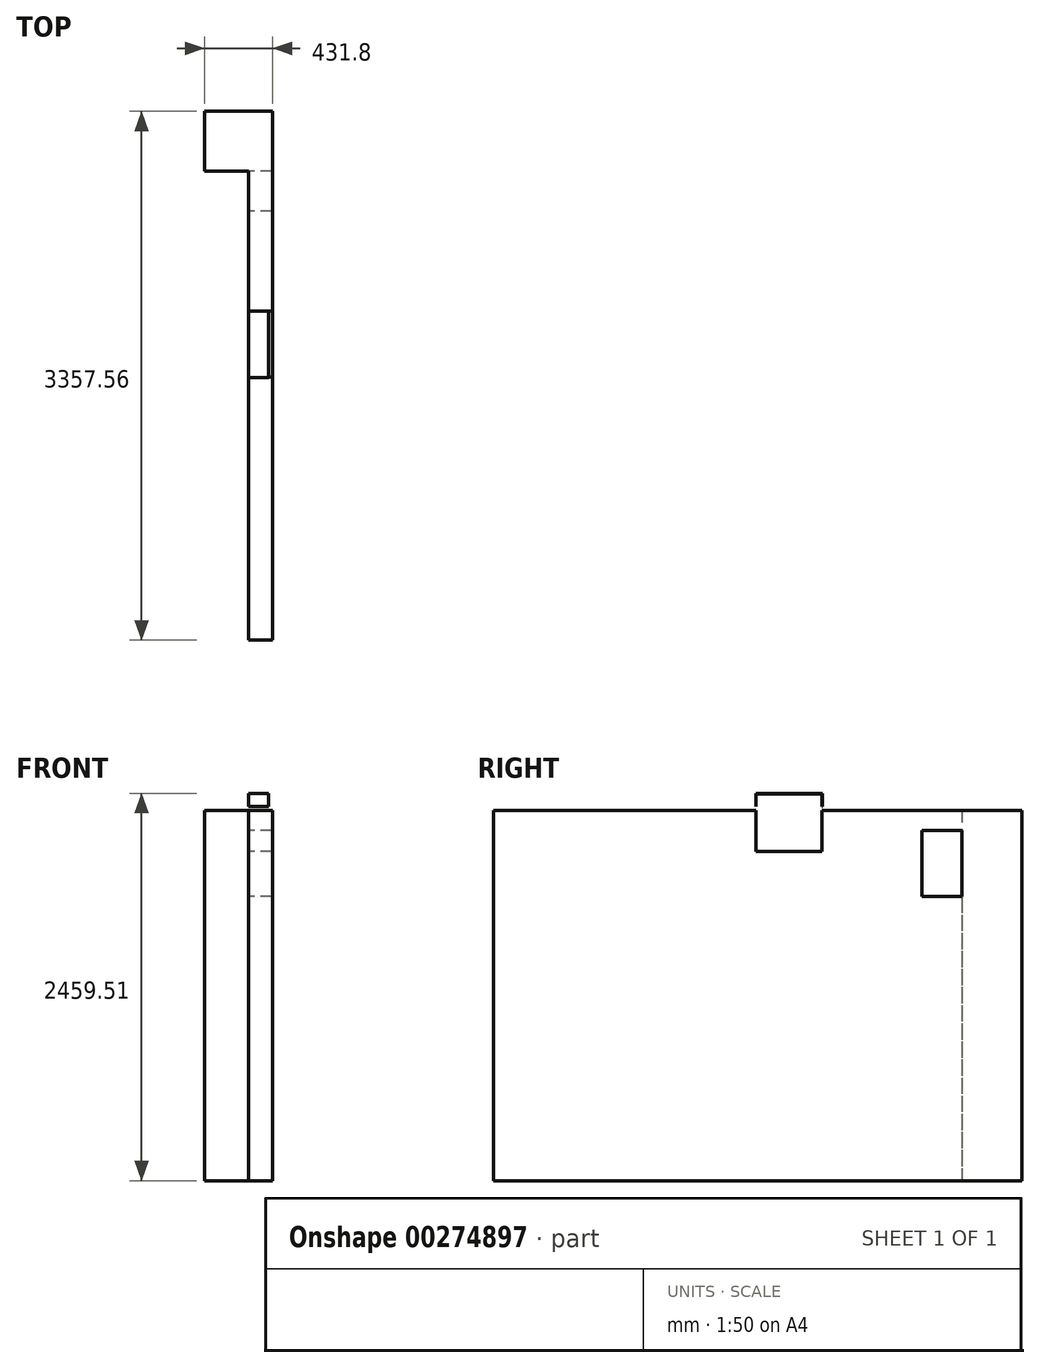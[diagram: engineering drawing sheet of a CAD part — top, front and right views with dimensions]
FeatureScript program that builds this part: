
annotation { "Feature Type Name" : "Feature", "Feature Type Description" : "" }
export const myFeature = defineFeature(function(context is Context, id is Id, definition is map)
    precondition{}
    {
        {
            var Q0;
            Q0=qCreatedBy(makeId("Top.planeOp"),FACE);
            var sketch = newSketch(context, id + "F0", { "sketchPlane" : qUnion([Q0])});
            skLineSegment(sketch, "E0.bottom", {"start": v(0, 0) * mm, "end": v(18288, 0) * mm});
            skLineSegment(sketch, "E0.top", {"start": v(0, 5486.4) * mm, "end": v(18288, 5486.4) * mm});
            skLineSegment(sketch, "E0.left", {"start": v(0, 0) * mm, "end": v(0, 5486.4) * mm});
            skLineSegment(sketch, "E0.right", {"start": v(18288, 0) * mm, "end": v(18288, 5486.4) * mm});
            skSolve(sketch);
        }
        {
            var Q0;
            Q0=makeQuery(id+"F0.imprint","IMPRINT",FACE,{"disambiguationData":[TD([[makeQuery(id+"F0.imprint","IMPRINT",EDGE,{"derivedFrom":sQuery(id+"F0.wireOp",EDGE,"E0.bottom")}),1.0]])]});
            extrude(context, id + "F1", {"entities" : qUnion([Q0]), "depth" : 101.6 * mm});
        }
        {
            var Q0;
            Q0=makeQuery(id+"F1.opExtrude","CAP_FACE",FACE,{"disambiguationData":[OSD([sQuery(id+"F0.wireOp",EDGE,"E0.bottom"),sQuery(id+"F0.wireOp",EDGE,"E0.top"),sQuery(id+"F0.wireOp",EDGE,"E0.left"),sQuery(id+"F0.wireOp",EDGE,"E0.right")])],"isStart":false});
            var sketch = newSketch(context, id + "F2", { "sketchPlane" : qUnion([Q0])});
            skLineSegment(sketch, "E1.bottom", {"start": v(18288, 5486.4) * mm, "end": v(13335, 5486.4) * mm, "construction": true});
            skLineSegment(sketch, "E1.top", {"start": v(18288, 2128.84) * mm, "end": v(13335, 2128.84) * mm, "construction": true});
            skLineSegment(sketch, "E1.left", {"start": v(18288, 5486.4) * mm, "end": v(18288, 2128.84) * mm, "construction": true});
            skLineSegment(sketch, "E1.right", {"start": v(13335, 5486.4) * mm, "end": v(13335, 2128.84) * mm, "construction": true});
            skLineSegment(sketch, "E2.bottom", {"start": v(18288, 2128.84) * mm, "end": v(13335, 2128.84) * mm});
            skLineSegment(sketch, "E2.top", {"start": v(18288, 1976.44) * mm, "end": v(13335, 1976.44) * mm});
            skLineSegment(sketch, "E2.left", {"start": v(18288, 2128.84) * mm, "end": v(18288, 1976.44) * mm});
            skLineSegment(sketch, "E2.right", {"start": v(13335, 2128.84) * mm, "end": v(13335, 1976.44) * mm});
            skLineSegment(sketch, "E3.bottom", {"start": v(13335, 5486.4) * mm, "end": v(13182.6, 5486.4) * mm});
            skLineSegment(sketch, "E3.top", {"start": v(13335, 2128.84) * mm, "end": v(13182.6, 2128.84) * mm});
            skLineSegment(sketch, "E3.left", {"start": v(13335, 5486.4) * mm, "end": v(13335, 2128.84) * mm});
            skLineSegment(sketch, "E3.right", {"start": v(13182.6, 5486.4) * mm, "end": v(13182.6, 2128.84) * mm});
            skLineSegment(sketch, "E4.bottom", {"start": v(13335, 1976.44) * mm, "end": v(13182.6, 1976.44) * mm});
            skLineSegment(sketch, "E4.left", {"start": v(13335, 1976.44) * mm, "end": v(13335, 2128.84) * mm});
            skLineSegment(sketch, "E4.right", {"start": v(13182.6, 1976.44) * mm, "end": v(13182.6, 2128.84) * mm});
            skSolve(sketch);
        }
        {
            var Q0;
            Q0=makeQuery(id+"F2.imprint","IMPRINT",FACE,{"disambiguationData":[TD([[makeQuery(id+"F2.imprint","IMPRINT",EDGE,{"derivedFrom":sQuery(id+"F2.wireOp",EDGE,"E2.bottom")}),1.0]])]});
            var Q1;
            Q1=makeQuery(id+"F2.imprint","IMPRINT",FACE,{"disambiguationData":[TD([[makeQuery(id+"F2.imprint","IMPRINT",EDGE,{"derivedFrom":sQuery(id+"F2.wireOp",EDGE,"E3.bottom")}),-1.0]])]});
            var Q2;
            Q2=makeQuery(id+"F2.imprint","IMPRINT",FACE,{"disambiguationData":[TD([[makeQuery(id+"F2.imprint","IMPRINT",EDGE,{"derivedFrom":sQuery(id+"F2.wireOp",EDGE,"E4.bottom")}),-1.0]])]});
            extrude(context, id + "F3", {"entities" : qUnion([Q0, Q1, Q2]), "operationType" : NewBodyOperationType.ADD, "depth" : 2426.5 * mm});
        }
        {
            var Q0;
            Q0=makeQuery(id+"F3.boolean.opBoolean","MERGE",FACE,{"derivedFrom":[makeQuery(id+"F1.opExtrude","SWEPT_FACE",FACE,{"disambiguationData":[OSD([sQuery(id+"F0.wireOp",EDGE,"E0.right")])]}),makeQuery(id+"F3.opExtrude","SWEPT_FACE",FACE,{"disambiguationData":[OSD([sQuery(id+"F2.wireOp",EDGE,"E2.left")])]})]});
            extrude(context, id + "F4", {"entities" : qUnion([Q0]), "operationType" : NewBodyOperationType.ADD, "depth" : 152.4 * mm});
        }
        {
            var Q0;
            {var subQ0=sQuery(id+"F0.wireOp",EDGE,"E0.top");Q0=makeQuery(id+"F4.boolean.opBoolean","MERGE",FACE,{"derivedFrom":[makeQuery(id+"F3.boolean.opBoolean","MERGE",FACE,{"derivedFrom":[makeQuery(id+"F1.opExtrude","SWEPT_FACE",FACE,{"disambiguationData":[OSD([subQ0])]}),makeQuery(id+"F3.opExtrude","SWEPT_FACE",FACE,{"disambiguationData":[OSD([sQuery(id+"F2.wireOp",EDGE,"E3.bottom")])]})]}),makeQuery(id+"F4.opExtrude","SWEPT_FACE",FACE,{"disambiguationData":[OSD([subQ0,sQuery(id+"F0.wireOp",EDGE,"E0.right")])]})]});}
            extrude(context, id + "F5", {"entities" : qUnion([Q0]), "operationType" : NewBodyOperationType.ADD, "depth" : 152.4 * mm});
        }
        {
            var Q0;
            {var subQ0=sQuery(id+"F0.wireOp",EDGE,"E0.right");var subQ1=sQuery(id+"F0.wireOp",EDGE,"E0.top");var subQ3=makeQuery(id+"F1.opExtrude","SWEPT_FACE",FACE,{"disambiguationData":[OSD([subQ0])]});var subQ4=makeQuery(id+"F1.opExtrude","SWEPT_FACE",FACE,{"disambiguationData":[OSD([subQ1])]});var subQ5=makeQuery(id+"F1.opExtrude","CAP_FACE",FACE,{"disambiguationData":[OSD([sQuery(id+"F0.wireOp",EDGE,"E0.bottom"),subQ1,sQuery(id+"F0.wireOp",EDGE,"E0.left"),subQ0])],"isStart":false});var subQ8=makeQuery(id+"F3.opExtrude","SWEPT_FACE",FACE,{"disambiguationData":[OSD([sQuery(id+"F2.wireOp",EDGE,"E2.bottom")])]});Q0=makeQuery(id+"F5.boolean.opBoolean","MERGE",FACE,{"derivedFrom":[makeQuery(id+"F4.boolean.opBoolean","MERGE",FACE,{"derivedFrom":[makeQuery(id+"F3.boolean.opBoolean","SPLIT",FACE,{"disambiguationData":[TD([subQ8])],"derivedFrom":subQ5}),makeQuery(id+"F4.opExtrude","SWEPT_FACE",FACE,{"disambiguationData":[OSD([subQ0]),TDD([makeQuery(id+"F3.boolean.opBoolean","SPLIT",EDGE,{"disambiguationData":[TD([subQ4])],"derivedFrom":makeQuery(id+"F1.opExtrude","CAP_EDGE",EDGE,{"disambiguationData":[OSD([subQ0])],"isStart":false})})])]})]}),makeQuery(id+"F5.opExtrude","SWEPT_FACE",FACE,{"disambiguationData":[OSD([subQ1,subQ0]),TDD([makeQuery(id+"F4.boolean.opBoolean","MERGE",EDGE,{"derivedFrom":[makeQuery(id+"F3.boolean.opBoolean","SPLIT",EDGE,{"disambiguationData":[TD([subQ3])],"derivedFrom":makeQuery(id+"F1.opExtrude","CAP_EDGE",EDGE,{"disambiguationData":[OSD([subQ1])],"isStart":false})}),makeQuery(id+"F4.opExtrude","SWEPT_EDGE",EDGE,{"disambiguationData":[OSD([subQ1,subQ0]),TDD([makeQuery(id+"F1.opExtrude","CAP_VERTEX",VERTEX,{"disambiguationData":[OSD([subQ1,subQ0])],"isStart":false})])]})]})])]})]});}
            var sketch = newSketch(context, id + "F6", { "sketchPlane" : qUnion([Q0])});
            skLineSegment(sketch, "E5.bottom", {"start": v(18440.4, 2128.84) * mm, "end": v(18288, 2128.84) * mm});
            skLineSegment(sketch, "E5.top", {"start": v(18440.4, 5638.8) * mm, "end": v(18288, 5638.8) * mm});
            skLineSegment(sketch, "E5.left", {"start": v(18440.4, 2128.84) * mm, "end": v(18440.4, 5638.8) * mm});
            skLineSegment(sketch, "E5.right", {"start": v(18288, 2128.84) * mm, "end": v(18288, 5638.8) * mm});
            skLineSegment(sketch, "E6.bottom", {"start": v(13335, 5638.8) * mm, "end": v(18288, 5638.8) * mm});
            skLineSegment(sketch, "E6.top", {"start": v(13335, 5486.4) * mm, "end": v(18288, 5486.4) * mm});
            skLineSegment(sketch, "E6.left", {"start": v(13335, 5638.8) * mm, "end": v(13335, 5486.4) * mm});
            skLineSegment(sketch, "E6.right", {"start": v(18288, 5638.8) * mm, "end": v(18288, 5486.4) * mm});
            skSolve(sketch);
        }
        {
            var Q0;
            Q0=makeQuery(id+"F6.imprint","IMPRINT",FACE,{"disambiguationData":[TD([[makeQuery(id+"F6.imprint","IMPRINT",EDGE,{"derivedFrom":sQuery(id+"F6.wireOp",EDGE,"E6.bottom")}),-1.0]])]});
            var Q1;
            Q1=makeQuery(id+"F6.imprint","IMPRINT",FACE,{"disambiguationData":[TD([[makeQuery(id+"F6.imprint","IMPRINT",EDGE,{"derivedFrom":sQuery(id+"F6.wireOp",EDGE,"E5.bottom")}),-1.0]])]});
            extrude(context, id + "F7", {"entities" : qUnion([Q0, Q1]), "operationType" : NewBodyOperationType.ADD, "depth" : 2350.3 * mm});
        }
        {
            var Q0;
            {var subQ0=sQuery(id+"F2.wireOp",EDGE,"E3.bottom");var subQ1=sQuery(id+"F2.wireOp",EDGE,"E2.left");Q0=makeQuery(id+"F5.boolean.opBoolean","MERGE",FACE,{"derivedFrom":[makeQuery(id+"F4.boolean.opBoolean","MERGE",FACE,{"derivedFrom":[makeQuery(id+"F3.opExtrude","CAP_FACE",FACE,{"disambiguationData":[OSD([sQuery(id+"F2.wireOp",EDGE,"E2.bottom"),sQuery(id+"F2.wireOp",EDGE,"E2.top"),subQ1,subQ0,sQuery(id+"F2.wireOp",EDGE,"E3.left"),sQuery(id+"F2.wireOp",EDGE,"E3.right"),sQuery(id+"F2.wireOp",EDGE,"E4.bottom"),sQuery(id+"F2.wireOp",EDGE,"E4.right")])],"isStart":false}),makeQuery(id+"F4.opExtrude","SWEPT_FACE",FACE,{"disambiguationData":[OSD([subQ1])]})]}),makeQuery(id+"F5.opExtrude","SWEPT_FACE",FACE,{"disambiguationData":[OSD([subQ0])]})]});}
            extrude(context, id + "F8", {"entities" : qUnion([Q0]), "operationType" : NewBodyOperationType.REMOVE, "oppositeDirection" : true, "depth" : 76.2 * mm});
        }
        {
            var Q0;
            {var subQ0=sQuery(id+"F0.wireOp",EDGE,"E0.right");var subQ1=sQuery(id+"F0.wireOp",EDGE,"E0.top");var subQ3=makeQuery(id+"F1.opExtrude","SWEPT_FACE",FACE,{"disambiguationData":[OSD([subQ0])]});var subQ4=makeQuery(id+"F1.opExtrude","SWEPT_FACE",FACE,{"disambiguationData":[OSD([subQ1])]});var subQ5=makeQuery(id+"F1.opExtrude","CAP_FACE",FACE,{"disambiguationData":[OSD([sQuery(id+"F0.wireOp",EDGE,"E0.bottom"),subQ1,sQuery(id+"F0.wireOp",EDGE,"E0.left"),subQ0])],"isStart":false});var subQ8=makeQuery(id+"F3.opExtrude","SWEPT_FACE",FACE,{"disambiguationData":[OSD([sQuery(id+"F2.wireOp",EDGE,"E2.bottom")])]});Q0=makeQuery(id+"F5.boolean.opBoolean","MERGE",FACE,{"derivedFrom":[makeQuery(id+"F4.boolean.opBoolean","MERGE",FACE,{"derivedFrom":[makeQuery(id+"F3.boolean.opBoolean","SPLIT",FACE,{"disambiguationData":[TD([subQ8])],"derivedFrom":subQ5}),makeQuery(id+"F4.opExtrude","SWEPT_FACE",FACE,{"disambiguationData":[OSD([subQ0]),TDD([makeQuery(id+"F3.boolean.opBoolean","SPLIT",EDGE,{"disambiguationData":[TD([subQ4])],"derivedFrom":makeQuery(id+"F1.opExtrude","CAP_EDGE",EDGE,{"disambiguationData":[OSD([subQ0])],"isStart":false})})])]})]}),makeQuery(id+"F5.opExtrude","SWEPT_FACE",FACE,{"disambiguationData":[OSD([subQ1,subQ0]),TDD([makeQuery(id+"F4.boolean.opBoolean","MERGE",EDGE,{"derivedFrom":[makeQuery(id+"F3.boolean.opBoolean","SPLIT",EDGE,{"disambiguationData":[TD([subQ3])],"derivedFrom":makeQuery(id+"F1.opExtrude","CAP_EDGE",EDGE,{"disambiguationData":[OSD([subQ1])],"isStart":false})}),makeQuery(id+"F4.opExtrude","SWEPT_EDGE",EDGE,{"disambiguationData":[OSD([subQ1,subQ0]),TDD([makeQuery(id+"F1.opExtrude","CAP_VERTEX",VERTEX,{"disambiguationData":[OSD([subQ1,subQ0])],"isStart":false})])]})]})])]})]});}
            var sketch = newSketch(context, id + "F9", { "sketchPlane" : qUnion([Q0])});
            skLineSegment(sketch, "E7.bottom", {"start": v(18288, 5486.4) * mm, "end": v(17907, 5486.4) * mm});
            skLineSegment(sketch, "E7.top", {"start": v(18288, 5207) * mm, "end": v(17907, 5207) * mm});
            skLineSegment(sketch, "E7.left", {"start": v(18288, 5486.4) * mm, "end": v(18288, 5207) * mm});
            skLineSegment(sketch, "E7.right", {"start": v(17907, 5486.4) * mm, "end": v(17907, 5207) * mm});
            skSolve(sketch);
        }
        {
            var Q0;
            Q0=makeQuery(id+"F9.imprint","IMPRINT",FACE,{"disambiguationData":[TD([[makeQuery(id+"F9.imprint","IMPRINT",EDGE,{"derivedFrom":sQuery(id+"F9.wireOp",EDGE,"E7.bottom")}),-1.0]])]});
            var Q1;
            Q1=makeQuery(id+"F8.boolean.opBoolean","MERGE",FACE,{"derivedFrom":[makeQuery(id+"F7.opExtrude","CAP_FACE",FACE,{"disambiguationData":[OSD([sQuery(id+"F6.wireOp",EDGE,"E5.bottom"),sQuery(id+"F6.wireOp",EDGE,"E5.top"),sQuery(id+"F6.wireOp",EDGE,"E5.left"),sQuery(id+"F6.wireOp",EDGE,"E5.right"),sQuery(id+"F6.wireOp",EDGE,"E6.bottom"),sQuery(id+"F6.wireOp",EDGE,"E6.top"),sQuery(id+"F6.wireOp",EDGE,"E6.left")])],"isStart":false}),makeQuery(id+"F8.opExtrude","CAP_FACE",FACE,{"disambiguationData":[OSD([sQuery(id+"F2.wireOp",EDGE,"E2.bottom"),sQuery(id+"F2.wireOp",EDGE,"E2.top"),sQuery(id+"F2.wireOp",EDGE,"E2.left"),sQuery(id+"F2.wireOp",EDGE,"E3.bottom"),sQuery(id+"F2.wireOp",EDGE,"E3.left"),sQuery(id+"F2.wireOp",EDGE,"E3.right"),sQuery(id+"F2.wireOp",EDGE,"E4.bottom"),sQuery(id+"F2.wireOp",EDGE,"E4.right")])],"isStart":false})]});
            extrude(context, id + "F10", {"entities" : qUnion([Q0]), "operationType" : NewBodyOperationType.ADD, "endBound" : BoundingType.UP_TO_SURFACE, "endBoundEntityFace" : qUnion([Q1]), "depth" : 25.4 * mm});
        }
        {
            var Q0;
            Q0=makeQuery(id+"F10.opExtrude","SWEPT_FACE",FACE,{"disambiguationData":[OSD([sQuery(id+"F9.wireOp",EDGE,"E7.top")])]});
            extrude(context, id + "F11", {"entities" : qUnion([Q0]), "operationType" : NewBodyOperationType.ADD, "depth" : 101.6 * mm});
        }
        {
            var Q0;
            {var subQ0=sQuery(id+"F9.wireOp",EDGE,"E7.right");Q0=makeQuery(id+"F11.boolean.opBoolean","MERGE",FACE,{"derivedFrom":[makeQuery(id+"F10.opExtrude","SWEPT_FACE",FACE,{"disambiguationData":[OSD([subQ0])]}),makeQuery(id+"F11.opExtrude","SWEPT_FACE",FACE,{"disambiguationData":[OSD([sQuery(id+"F9.wireOp",EDGE,"E7.top"),subQ0])]})]});}
            extrude(context, id + "F12", {"entities" : qUnion([Q0]), "operationType" : NewBodyOperationType.REMOVE, "oppositeDirection" : true, "depth" : 101.6 * mm});
        }
        {
            var Q0;
            {var subQ0=sQuery(id+"F2.wireOp",EDGE,"E3.right");Q0=makeQuery(id+"F5.boolean.opBoolean","MERGE",FACE,{"derivedFrom":[makeQuery(id+"F3.opExtrude","SWEPT_FACE",FACE,{"disambiguationData":[OSD([subQ0,sQuery(id+"F2.wireOp",EDGE,"E4.right")])]}),makeQuery(id+"F5.opExtrude","SWEPT_FACE",FACE,{"disambiguationData":[OSD([sQuery(id+"F0.wireOp",EDGE,"E0.top"),sQuery(id+"F2.wireOp",EDGE,"E3.bottom"),subQ0])]})]});}
            extrude(context, id + "F13", {"entities" : qUnion([Q0]), "operationType" : NewBodyOperationType.ADD, "depth" : 275.43 * mm});
        }
        {
            var Q0;
            {var subQ0=sQuery(id+"F2.wireOp",EDGE,"E3.left");Q0=makeQuery(id+"F5.boolean.opBoolean","MERGE",FACE,{"derivedFrom":[makeQuery(id+"F3.opExtrude","SWEPT_FACE",FACE,{"disambiguationData":[OSD([subQ0])]}),makeQuery(id+"F5.opExtrude","SWEPT_FACE",FACE,{"disambiguationData":[OSD([sQuery(id+"F0.wireOp",EDGE,"E0.top"),sQuery(id+"F2.wireOp",EDGE,"E3.bottom"),subQ0])]})]});}
            extrude(context, id + "F14", {"entities" : qUnion([Q0]), "operationType" : NewBodyOperationType.REMOVE, "oppositeDirection" : true, "depth" : 275.43 * mm});
        }
        {
            var Q0;
            {var subQ0=sQuery(id+"F2.wireOp",EDGE,"E4.bottom");var subQ1=sQuery(id+"F2.wireOp",EDGE,"E2.top");Q0=makeQuery(id+"F13.boolean.opBoolean","MERGE",FACE,{"derivedFrom":[makeQuery(id+"F4.boolean.opBoolean","MERGE",FACE,{"derivedFrom":[makeQuery(id+"F3.opExtrude","SWEPT_FACE",FACE,{"disambiguationData":[OSD([subQ1,subQ0])]}),makeQuery(id+"F4.opExtrude","SWEPT_FACE",FACE,{"disambiguationData":[OSD([sQuery(id+"F0.wireOp",EDGE,"E0.right"),subQ1,sQuery(id+"F2.wireOp",EDGE,"E2.left")])]})]}),makeQuery(id+"F13.opExtrude","SWEPT_FACE",FACE,{"disambiguationData":[OSD([subQ0,sQuery(id+"F2.wireOp",EDGE,"E4.right")])]})]});}
            extrude(context, id + "F15", {"entities" : qUnion([Q0]), "operationType" : NewBodyOperationType.REMOVE, "oppositeDirection" : true, "depth" : 25.4 * mm});
        }
        {
            var Q0;
            {var subQ0=sQuery(id+"F2.wireOp",EDGE,"E2.bottom");Q0=makeQuery(id+"F14.boolean.opBoolean","MERGE",FACE,{"derivedFrom":[makeQuery(id+"F4.boolean.opBoolean","MERGE",FACE,{"derivedFrom":[makeQuery(id+"F3.opExtrude","SWEPT_FACE",FACE,{"disambiguationData":[OSD([subQ0])]}),makeQuery(id+"F4.opExtrude","SWEPT_FACE",FACE,{"disambiguationData":[OSD([sQuery(id+"F0.wireOp",EDGE,"E0.right"),subQ0,sQuery(id+"F2.wireOp",EDGE,"E2.left")])]})]}),makeQuery(id+"F14.opExtrude","SWEPT_FACE",FACE,{"disambiguationData":[OSD([subQ0,sQuery(id+"F2.wireOp",EDGE,"E3.left"),sQuery(id+"F2.wireOp",EDGE,"E3.top"),sQuery(id+"F2.wireOp",EDGE,"E4.left")])]})]});}
            var sketch = newSketch(context, id + "F16", { "sketchPlane" : qUnion([Q0])});
            skLineSegment(sketch, "E8.bottom", {"start": v(-13059.57, 2451.9) * mm, "end": v(-14431.17, 2451.9) * mm, "construction": true});
            skLineSegment(sketch, "E8.top", {"start": v(-13059.57, 2197.9) * mm, "end": v(-14431.17, 2197.9) * mm, "construction": true});
            skLineSegment(sketch, "E8.left", {"start": v(-13059.57, 2451.9) * mm, "end": v(-13059.57, 2197.9) * mm, "construction": true});
            skLineSegment(sketch, "E8.right", {"start": v(-14431.17, 2451.9) * mm, "end": v(-14431.17, 2197.9) * mm, "construction": true});
            skLineSegment(sketch, "E9.bottom", {"start": v(-14431.17, 2197.9) * mm, "end": v(-15193.17, 2197.9) * mm});
            skLineSegment(sketch, "E9.top", {"start": v(-14431.17, 1943.9) * mm, "end": v(-15193.17, 1943.9) * mm});
            skLineSegment(sketch, "E9.left", {"start": v(-14431.17, 2197.9) * mm, "end": v(-14431.17, 1943.9) * mm});
            skLineSegment(sketch, "E9.right", {"start": v(-15193.17, 2197.9) * mm, "end": v(-15193.17, 1943.9) * mm});
            skSolve(sketch);
        }
        {
            var Q0;
            Q0=makeQuery(id+"F16.imprint","IMPRINT",FACE,{"disambiguationData":[TD([[makeQuery(id+"F16.imprint","IMPRINT",EDGE,{"derivedFrom":sQuery(id+"F16.wireOp",EDGE,"E9.bottom")}),1.0]])]});
            extrude(context, id + "F17", {"entities" : qUnion([Q0]), "operationType" : NewBodyOperationType.REMOVE, "endBound" : BoundingType.THROUGH_ALL, "oppositeDirection" : true, "depth" : 25.4 * mm});
        }
        {
            var Q0;
            Q0=makeQuery(id+"F17.boolean.opBoolean","COPY",FACE,{"derivedFrom":makeQuery(id+"F17.opExtrude","SWEPT_FACE",FACE,{"disambiguationData":[OSD([sQuery(id+"F16.wireOp",EDGE,"E9.bottom")])]})});
            extrude(context, id + "F18", {"entities" : qUnion([Q0]), "operationType" : NewBodyOperationType.REMOVE, "oppositeDirection" : true, "depth" : 190.5 * mm});
        }
        {
            var Q0;
            Q0=makeQuery(id+"F17.boolean.opBoolean","COPY",FACE,{"derivedFrom":makeQuery(id+"F17.opExtrude","SWEPT_FACE",FACE,{"disambiguationData":[OSD([sQuery(id+"F16.wireOp",EDGE,"E9.top")])]})});
            extrude(context, id + "F19", {"entities" : qUnion([Q0]), "operationType" : NewBodyOperationType.ADD, "depth" : 63.5 * mm});
        }
        {
            var Q0;
            Q0=makeQuery(id+"F7.opExtrude","SWEPT_FACE",FACE,{"disambiguationData":[OSD([sQuery(id+"F6.wireOp",EDGE,"E5.right")])]});
            var sketch = newSketch(context, id + "F20", { "sketchPlane" : qUnion([Q0])});
            skLineSegment(sketch, "E10.bottom", {"start": v(-5105.4, 2451.9) * mm, "end": v(-4851.4, 2451.9) * mm, "construction": true});
            skLineSegment(sketch, "E10.top", {"start": v(-5105.4, 2375.7) * mm, "end": v(-4851.4, 2375.7) * mm, "construction": true});
            skLineSegment(sketch, "E10.left", {"start": v(-5105.4, 2451.9) * mm, "end": v(-5105.4, 2375.7) * mm, "construction": true});
            skLineSegment(sketch, "E10.right", {"start": v(-4851.4, 2451.9) * mm, "end": v(-4851.4, 2375.7) * mm, "construction": true});
            skLineSegment(sketch, "E11.bottom", {"start": v(-4851.4, 2375.7) * mm, "end": v(-5105.4, 2375.7) * mm});
            skLineSegment(sketch, "E11.top", {"start": v(-4851.4, 2070.9) * mm, "end": v(-5105.4, 2070.9) * mm});
            skLineSegment(sketch, "E11.left", {"start": v(-4851.4, 2375.7) * mm, "end": v(-4851.4, 2070.9) * mm});
            skLineSegment(sketch, "E11.right", {"start": v(-5105.4, 2375.7) * mm, "end": v(-5105.4, 2070.9) * mm});
            skSolve(sketch);
        }
        {
            var Q0;
            Q0=makeQuery(id+"F20.imprint","IMPRINT",FACE,{"disambiguationData":[TD([[makeQuery(id+"F20.imprint","IMPRINT",EDGE,{"derivedFrom":sQuery(id+"F20.wireOp",EDGE,"E11.bottom")}),1.0]])]});
            extrude(context, id + "F21", {"entities" : qUnion([Q0]), "operationType" : NewBodyOperationType.REMOVE, "endBound" : BoundingType.THROUGH_ALL, "oppositeDirection" : true, "depth" : 25.4 * mm});
        }
        {
            var Q0;
            Q0=makeQuery(id+"F7.opExtrude","SWEPT_FACE",FACE,{"disambiguationData":[OSD([sQuery(id+"F6.wireOp",EDGE,"E5.right")])]});
            var sketch = newSketch(context, id + "F22", { "sketchPlane" : qUnion([Q0])});
            skLineSegment(sketch, "E12.bottom", {"start": v(-4851.4, 2375.7) * mm, "end": v(-3606.8, 2375.7) * mm, "construction": true});
            skLineSegment(sketch, "E12.top", {"start": v(-4851.4, 2070.9) * mm, "end": v(-3606.8, 2070.9) * mm, "construction": true});
            skLineSegment(sketch, "E12.left", {"start": v(-4851.4, 2375.7) * mm, "end": v(-4851.4, 2070.9) * mm, "construction": true});
            skLineSegment(sketch, "E12.right", {"start": v(-3606.8, 2375.7) * mm, "end": v(-3606.8, 2070.9) * mm, "construction": true});
            skLineSegment(sketch, "E13.bottom", {"start": v(-3606.8, 2375.7) * mm, "end": v(-3888.54, 2375.7) * mm});
            skLineSegment(sketch, "E13.top", {"start": v(-3606.8, 2070.9) * mm, "end": v(-3888.54, 2070.9) * mm});
            skLineSegment(sketch, "E13.left", {"start": v(-3606.8, 2375.7) * mm, "end": v(-3606.8, 2070.9) * mm});
            skLineSegment(sketch, "E13.right", {"start": v(-3888.54, 2375.7) * mm, "end": v(-3888.54, 2070.9) * mm});
            skSolve(sketch);
        }
        {
            var Q0;
            Q0=makeQuery(id+"F22.imprint","IMPRINT",FACE,{"disambiguationData":[TD([[makeQuery(id+"F22.imprint","IMPRINT",EDGE,{"derivedFrom":sQuery(id+"F22.wireOp",EDGE,"E13.bottom")}),1.0]])]});
            extrude(context, id + "F23", {"entities" : qUnion([Q0]), "operationType" : NewBodyOperationType.REMOVE, "endBound" : BoundingType.THROUGH_ALL, "oppositeDirection" : true, "depth" : 25.4 * mm});
        }
        {
            var Q0;
            Q0=makeQuery(id+"F23.boolean.opBoolean","COPY",FACE,{"derivedFrom":makeQuery(id+"F23.opExtrude","SWEPT_FACE",FACE,{"disambiguationData":[OSD([sQuery(id+"F22.wireOp",EDGE,"E13.right")])]})});
            extrude(context, id + "F24", {"entities" : qUnion([Q0]), "operationType" : NewBodyOperationType.REMOVE, "oppositeDirection" : true, "depth" : 304.8 * mm});
        }
        {
            var Q0;
            Q0=makeQuery(id+"F23.boolean.opBoolean","COPY",FACE,{"derivedFrom":makeQuery(id+"F23.opExtrude","SWEPT_FACE",FACE,{"disambiguationData":[OSD([sQuery(id+"F22.wireOp",EDGE,"E13.left")])]})});
            extrude(context, id + "F25", {"entities" : qUnion([Q0]), "operationType" : NewBodyOperationType.ADD, "depth" : 304.8 * mm});
        }
        {
            var Q0;
            Q0=makeQuery(id+"F24.boolean.opBoolean","COPY",FACE,{"derivedFrom":makeQuery(id+"F24.opExtrude","CAP_FACE",FACE,{"disambiguationData":[OSD([sQuery(id+"F22.wireOp",EDGE,"E13.right")])],"isStart":false})});
            extrude(context, id + "F26", {"entities" : qUnion([Q0]), "operationType" : NewBodyOperationType.ADD, "depth" : 25.4 * mm});
        }
        {
            var Q0;
            Q0=makeQuery(id+"F25.opExtrude","CAP_FACE",FACE,{"disambiguationData":[OSD([sQuery(id+"F22.wireOp",EDGE,"E13.left")])],"isStart":false});
            extrude(context, id + "F27", {"entities" : qUnion([Q0]), "operationType" : NewBodyOperationType.REMOVE, "oppositeDirection" : true, "depth" : 25.4 * mm});
        }
        {
            var Q0;
            Q0=makeQuery(id+"F27.boolean.opBoolean","COPY",FACE,{"derivedFrom":makeQuery(id+"F27.opExtrude","CAP_FACE",FACE,{"disambiguationData":[OSD([sQuery(id+"F22.wireOp",EDGE,"E13.left")])],"isStart":false})});
            extrude(context, id + "F28", {"entities" : qUnion([Q0]), "operationType" : NewBodyOperationType.REMOVE, "oppositeDirection" : true, "depth" : 12.7 * mm});
        }
        {
            var Q0;
            Q0=makeQuery(id+"F26.opExtrude","CAP_FACE",FACE,{"disambiguationData":[OSD([sQuery(id+"F22.wireOp",EDGE,"E13.right")])],"isStart":false});
            extrude(context, id + "F29", {"entities" : qUnion([Q0]), "operationType" : NewBodyOperationType.ADD, "depth" : 12.7 * mm});
        }
        {
            var Q0;
            Q0=makeQuery(id+"F13.opExtrude","CAP_FACE",FACE,{"disambiguationData":[OSD([sQuery(id+"F0.wireOp",EDGE,"E0.top"),sQuery(id+"F2.wireOp",EDGE,"E3.bottom"),sQuery(id+"F2.wireOp",EDGE,"E3.right"),sQuery(id+"F2.wireOp",EDGE,"E4.right")])],"isStart":false});
            var sketch = newSketch(context, id + "F30", { "sketchPlane" : qUnion([Q0])});
            skLineSegment(sketch, "E14.bottom", {"start": v(-2001.84, 2451.9) * mm, "end": v(-2408.24, 2451.9) * mm, "construction": true});
            skLineSegment(sketch, "E14.top", {"start": v(-2001.84, 1527.67) * mm, "end": v(-2408.24, 1527.67) * mm, "construction": true});
            skLineSegment(sketch, "E14.left", {"start": v(-2001.84, 2451.9) * mm, "end": v(-2001.84, 1527.67) * mm, "construction": true});
            skLineSegment(sketch, "E14.right", {"start": v(-2408.24, 2451.9) * mm, "end": v(-2408.24, 1527.67) * mm, "construction": true});
            skLineSegment(sketch, "E15.bottom", {"start": v(-2408.24, 2451.9) * mm, "end": v(-2535.24, 2451.9) * mm});
            skLineSegment(sketch, "E15.top", {"start": v(-2408.24, 101.6) * mm, "end": v(-2535.24, 101.6) * mm});
            skLineSegment(sketch, "E15.left", {"start": v(-2408.24, 2451.9) * mm, "end": v(-2408.24, 101.6) * mm});
            skLineSegment(sketch, "E15.right", {"start": v(-2535.24, 2451.9) * mm, "end": v(-2535.24, 101.6) * mm});
            skSolve(sketch);
        }
        {
            var Q0;
            Q0=makeQuery(id+"F30.imprint","IMPRINT",FACE,{"disambiguationData":[TD([[makeQuery(id+"F30.imprint","IMPRINT",EDGE,{"derivedFrom":sQuery(id+"F30.wireOp",EDGE,"E15.bottom")}),-1.0]])]});
            var Q1;
            {var subQ0=sQuery(id+"F0.wireOp",EDGE,"E0.left");Q1=makeQuery(id+"F5.boolean.opBoolean","MERGE",FACE,{"derivedFrom":[makeQuery(id+"F1.opExtrude","SWEPT_FACE",FACE,{"disambiguationData":[OSD([subQ0])]}),makeQuery(id+"F5.opExtrude","SWEPT_FACE",FACE,{"disambiguationData":[OSD([sQuery(id+"F0.wireOp",EDGE,"E0.top"),subQ0])]})]});}
            extrude(context, id + "F31", {"entities" : qUnion([Q0]), "operationType" : NewBodyOperationType.ADD, "endBound" : BoundingType.UP_TO_SURFACE, "endBoundEntityFace" : qUnion([Q1]), "depth" : 25.4 * mm});
        }
        {
            var Q0;
            Q0=makeQuery(id+"F31.opExtrude","SWEPT_FACE",FACE,{"disambiguationData":[OSD([sQuery(id+"F30.wireOp",EDGE,"E15.left")])]});
            var sketch = newSketch(context, id + "F32", { "sketchPlane" : qUnion([Q0])});
            skLineSegment(sketch, "E16.bottom", {"start": v(12907.17, 101.6) * mm, "end": v(12805.57, 101.6) * mm, "construction": true});
            skLineSegment(sketch, "E16.top", {"start": v(12907.17, 469.78) * mm, "end": v(12805.57, 469.78) * mm, "construction": true});
            skLineSegment(sketch, "E16.left", {"start": v(12907.17, 101.6) * mm, "end": v(12907.17, 469.78) * mm, "construction": true});
            skLineSegment(sketch, "E16.right", {"start": v(12805.57, 101.6) * mm, "end": v(12805.57, 469.78) * mm, "construction": true});
            skLineSegment(sketch, "E17.bottom", {"start": v(12805.57, 101.6) * mm, "end": v(11230.77, 101.6) * mm});
            skLineSegment(sketch, "E17.top", {"start": v(12805.57, 2235.2) * mm, "end": v(11230.77, 2235.2) * mm});
            skLineSegment(sketch, "E17.left", {"start": v(12805.57, 101.6) * mm, "end": v(12805.57, 2235.2) * mm});
            skLineSegment(sketch, "E17.right", {"start": v(11230.77, 101.6) * mm, "end": v(11230.77, 2235.2) * mm});
            skSolve(sketch);
        }
        {
            var Q0;
            Q0=makeQuery(id+"F32.imprint","IMPRINT",FACE,{"disambiguationData":[TD([[makeQuery(id+"F32.imprint","IMPRINT",EDGE,{"derivedFrom":sQuery(id+"F32.wireOp",EDGE,"E17.bottom")}),1.0]])]});
            extrude(context, id + "F33", {"entities" : qUnion([Q0]), "operationType" : NewBodyOperationType.REMOVE, "endBound" : BoundingType.THROUGH_ALL, "oppositeDirection" : true, "depth" : 25.4 * mm});
        }
        {
            var Q0;
            Q0=makeQuery(id+"F33.boolean.opBoolean","COPY",FACE,{"derivedFrom":makeQuery(id+"F33.opExtrude","SWEPT_FACE",FACE,{"disambiguationData":[OSD([sQuery(id+"F32.wireOp",EDGE,"E17.right")])]})});
            extrude(context, id + "F34", {"entities" : qUnion([Q0]), "operationType" : NewBodyOperationType.REMOVE, "oppositeDirection" : true, "depth" : 1320.8 * mm});
        }
        {
            var Q0;
            Q0=makeQuery(id+"F33.boolean.opBoolean","COPY",FACE,{"derivedFrom":makeQuery(id+"F33.opExtrude","SWEPT_FACE",FACE,{"disambiguationData":[OSD([sQuery(id+"F32.wireOp",EDGE,"E17.left")])]})});
            extrude(context, id + "F35", {"entities" : qUnion([Q0]), "operationType" : NewBodyOperationType.ADD, "depth" : 1320.8 * mm});
        }
        {
            var Q0;
            {var subQ0=sQuery(id+"F22.wireOp",EDGE,"E13.left");var subQ1=sQuery(id+"F22.wireOp",EDGE,"E13.top");Q0=makeQuery(id+"F28.boolean.opBoolean","MERGE",FACE,{"derivedFrom":[makeQuery(id+"F27.boolean.opBoolean","MERGE",FACE,{"derivedFrom":[makeQuery(id+"F24.boolean.opBoolean","MERGE",FACE,{"derivedFrom":[makeQuery(id+"F23.boolean.opBoolean","COPY",FACE,{"derivedFrom":makeQuery(id+"F23.opExtrude","SWEPT_FACE",FACE,{"disambiguationData":[OSD([subQ1])]})}),makeQuery(id+"F24.opExtrude","SWEPT_FACE",FACE,{"disambiguationData":[OSD([subQ1,sQuery(id+"F22.wireOp",EDGE,"E13.right")])]})]}),makeQuery(id+"F27.opExtrude","SWEPT_FACE",FACE,{"disambiguationData":[OSD([subQ1,subQ0])]})]}),makeQuery(id+"F28.opExtrude","SWEPT_FACE",FACE,{"disambiguationData":[OSD([subQ1,subQ0])]})]});}
            extrude(context, id + "F36", {"entities" : qUnion([Q0]), "operationType" : NewBodyOperationType.ADD, "depth" : 120.65 * mm});
        }
        {
            var Q0;
            {var subQ0=sQuery(id+"F22.wireOp",EDGE,"E13.left");var subQ1=sQuery(id+"F22.wireOp",EDGE,"E13.bottom");Q0=makeQuery(id+"F28.boolean.opBoolean","MERGE",FACE,{"derivedFrom":[makeQuery(id+"F27.boolean.opBoolean","MERGE",FACE,{"derivedFrom":[makeQuery(id+"F24.boolean.opBoolean","MERGE",FACE,{"derivedFrom":[makeQuery(id+"F23.boolean.opBoolean","COPY",FACE,{"derivedFrom":makeQuery(id+"F23.opExtrude","SWEPT_FACE",FACE,{"disambiguationData":[OSD([subQ1])]})}),makeQuery(id+"F24.opExtrude","SWEPT_FACE",FACE,{"disambiguationData":[OSD([subQ1,sQuery(id+"F22.wireOp",EDGE,"E13.right")])]})]}),makeQuery(id+"F27.opExtrude","SWEPT_FACE",FACE,{"disambiguationData":[OSD([subQ1,subQ0])]})]}),makeQuery(id+"F28.opExtrude","SWEPT_FACE",FACE,{"disambiguationData":[OSD([subQ1,subQ0])]})]});}
            extrude(context, id + "F37", {"entities" : qUnion([Q0]), "operationType" : NewBodyOperationType.REMOVE, "endBound" : BoundingType.THROUGH_ALL, "oppositeDirection" : true, "depth" : 25.4 * mm});
        }
        {
            var Q0;
            Q0=makeQuery(id+"F21.boolean.opBoolean","COPY",FACE,{"derivedFrom":makeQuery(id+"F21.opExtrude","SWEPT_FACE",FACE,{"disambiguationData":[OSD([sQuery(id+"F20.wireOp",EDGE,"E11.top")])]})});
            extrude(context, id + "F38", {"entities" : qUnion([Q0]), "operationType" : NewBodyOperationType.REMOVE, "oppositeDirection" : true, "depth" : 190.5 * mm});
        }
        {
            var Q0;
            Q0=makeQuery(id+"F21.boolean.opBoolean","COPY",FACE,{"derivedFrom":makeQuery(id+"F21.opExtrude","SWEPT_FACE",FACE,{"disambiguationData":[OSD([sQuery(id+"F20.wireOp",EDGE,"E11.bottom")])]})});
            extrude(context, id + "F39", {"entities" : qUnion([Q0]), "operationType" : NewBodyOperationType.ADD, "depth" : 190.5 * mm});
        }
        {
            var Q0;
            Q0=makeQuery(id+"F39.opExtrude","CAP_FACE",FACE,{"disambiguationData":[OSD([sQuery(id+"F20.wireOp",EDGE,"E11.bottom")])],"isStart":false});
            extrude(context, id + "F40", {"entities" : qUnion([Q0]), "operationType" : NewBodyOperationType.REMOVE, "oppositeDirection" : true, "depth" : 76.2 * mm});
        }
        {
            var Q0;
            {var subQ0=sQuery(id+"F16.wireOp",EDGE,"E9.right");Q0=makeQuery(id+"F18.boolean.opBoolean","MERGE",FACE,{"derivedFrom":[makeQuery(id+"F17.boolean.opBoolean","COPY",FACE,{"derivedFrom":makeQuery(id+"F17.opExtrude","SWEPT_FACE",FACE,{"disambiguationData":[OSD([subQ0])]})}),makeQuery(id+"F18.opExtrude","SWEPT_FACE",FACE,{"disambiguationData":[OSD([sQuery(id+"F16.wireOp",EDGE,"E9.bottom"),subQ0])]})]});}
            extrude(context, id + "F41", {"entities" : qUnion([Q0]), "operationType" : NewBodyOperationType.REMOVE, "oppositeDirection" : true, "depth" : 406.4 * mm});
        }
        {
            var Q0;
            {var subQ0=sQuery(id+"F16.wireOp",EDGE,"E9.left");Q0=makeQuery(id+"F18.boolean.opBoolean","MERGE",FACE,{"derivedFrom":[makeQuery(id+"F17.boolean.opBoolean","COPY",FACE,{"derivedFrom":makeQuery(id+"F17.opExtrude","SWEPT_FACE",FACE,{"disambiguationData":[OSD([subQ0])]})}),makeQuery(id+"F18.opExtrude","SWEPT_FACE",FACE,{"disambiguationData":[OSD([sQuery(id+"F16.wireOp",EDGE,"E9.bottom"),subQ0])]})]});}
            extrude(context, id + "F42", {"entities" : qUnion([Q0]), "operationType" : NewBodyOperationType.ADD, "depth" : 406.4 * mm});
        }
        {
            var Q0;
            {var subQ0=sQuery(id+"F22.wireOp",EDGE,"E13.left");Q0=makeQuery(id+"F37.boolean.opBoolean","MERGE",FACE,{"derivedFrom":[makeQuery(id+"F28.boolean.opBoolean","COPY",FACE,{"derivedFrom":makeQuery(id+"F28.opExtrude","CAP_FACE",FACE,{"disambiguationData":[OSD([subQ0])],"isStart":false})}),makeQuery(id+"F37.opExtrude","SWEPT_FACE",FACE,{"disambiguationData":[OSD([sQuery(id+"F22.wireOp",EDGE,"E13.bottom"),subQ0])]})]});}
            extrude(context, id + "F43", {"entities" : qUnion([Q0]), "operationType" : NewBodyOperationType.REMOVE, "oppositeDirection" : true, "depth" : 76.2 * mm});
        }
        {
            var Q0;
            {var subQ0=sQuery(id+"F22.wireOp",EDGE,"E13.right");Q0=makeQuery(id+"F37.boolean.opBoolean","MERGE",FACE,{"derivedFrom":[makeQuery(id+"F29.opExtrude","CAP_FACE",FACE,{"disambiguationData":[OSD([subQ0])],"isStart":false}),makeQuery(id+"F37.opExtrude","SWEPT_FACE",FACE,{"disambiguationData":[OSD([sQuery(id+"F22.wireOp",EDGE,"E13.bottom"),subQ0])]})]});}
            extrude(context, id + "F44", {"entities" : qUnion([Q0]), "operationType" : NewBodyOperationType.REMOVE, "oppositeDirection" : true, "depth" : 60.96 * mm});
        }
        {
            var Q0;
            Q0=makeQuery(id+"F38.boolean.opBoolean","COPY",FACE,{"derivedFrom":makeQuery(id+"F38.opExtrude","CAP_FACE",FACE,{"disambiguationData":[OSD([sQuery(id+"F20.wireOp",EDGE,"E11.top")])],"isStart":false})});
            extrude(context, id + "F45", {"entities" : qUnion([Q0]), "operationType" : NewBodyOperationType.ADD, "depth" : 25.4 * mm});
        }
        {
            var Q0;
            Q0=makeQuery(id+"F40.boolean.opBoolean","COPY",FACE,{"derivedFrom":makeQuery(id+"F40.opExtrude","CAP_FACE",FACE,{"disambiguationData":[OSD([sQuery(id+"F20.wireOp",EDGE,"E11.bottom")])],"isStart":false})});
            extrude(context, id + "F46", {"entities" : qUnion([Q0]), "operationType" : NewBodyOperationType.REMOVE, "oppositeDirection" : true, "depth" : 63.5 * mm});
        }
        {
            var Q0;
            {var subQ0=sQuery(id+"F0.wireOp",EDGE,"E0.right");var subQ1=sQuery(id+"F0.wireOp",EDGE,"E0.top");Q0=makeQuery(id+"F5.boolean.opBoolean","MERGE",FACE,{"derivedFrom":[makeQuery(id+"F4.boolean.opBoolean","MERGE",FACE,{"derivedFrom":[makeQuery(id+"F1.opExtrude","CAP_FACE",FACE,{"disambiguationData":[OSD([sQuery(id+"F0.wireOp",EDGE,"E0.bottom"),subQ1,sQuery(id+"F0.wireOp",EDGE,"E0.left"),subQ0])],"isStart":true}),makeQuery(id+"F4.opExtrude","SWEPT_FACE",FACE,{"disambiguationData":[OSD([subQ0]),TDD([makeQuery(id+"F1.opExtrude","CAP_EDGE",EDGE,{"disambiguationData":[OSD([subQ0])],"isStart":true})])]})]}),makeQuery(id+"F5.opExtrude","SWEPT_FACE",FACE,{"disambiguationData":[OSD([subQ1,subQ0]),TDD([makeQuery(id+"F4.boolean.opBoolean","MERGE",EDGE,{"derivedFrom":[makeQuery(id+"F1.opExtrude","CAP_EDGE",EDGE,{"disambiguationData":[OSD([subQ1])],"isStart":true}),makeQuery(id+"F4.opExtrude","SWEPT_EDGE",EDGE,{"disambiguationData":[OSD([subQ1,subQ0]),TDD([makeQuery(id+"F1.opExtrude","CAP_VERTEX",VERTEX,{"disambiguationData":[OSD([subQ1,subQ0])],"isStart":true})])]})]})])]})]});}
            var Q1;
            {var subQ0=sQuery(id+"F32.wireOp",EDGE,"E17.bottom");var subQ1=sQuery(id+"F30.wireOp",EDGE,"E15.left");var subQ2=sQuery(id+"F2.wireOp",EDGE,"E4.right");var subQ3=sQuery(id+"F2.wireOp",EDGE,"E3.right");var subQ4=sQuery(id+"F2.wireOp",EDGE,"E3.bottom");var subQ5=sQuery(id+"F0.wireOp",EDGE,"E0.top");var subQ6=sQuery(id+"F0.wireOp",EDGE,"E0.right");var subQ7=sQuery(id+"F0.wireOp",EDGE,"E0.left");var subQ12=sQuery(id+"F2.wireOp",EDGE,"E4.bottom");var subQ13=sQuery(id+"F2.wireOp",EDGE,"E2.left");var subQ14=sQuery(id+"F2.wireOp",EDGE,"E2.top");var subQ16=sQuery(id+"F0.wireOp",EDGE,"E0.bottom");var subQ17=makeQuery(id+"F1.opExtrude","CAP_FACE",FACE,{"disambiguationData":[OSD([subQ16,subQ5,subQ7,subQ6])],"isStart":false});var subQ20=makeQuery(id+"F1.opExtrude","SWEPT_FACE",FACE,{"disambiguationData":[OSD([subQ16])]});var subQ21=makeQuery(id+"F15.boolean.opBoolean","MERGE",FACE,{"derivedFrom":[makeQuery(id+"F5.boolean.opBoolean","MERGE",FACE,{"derivedFrom":[makeQuery(id+"F4.boolean.opBoolean","MERGE",FACE,{"derivedFrom":[makeQuery(id+"F3.boolean.opBoolean","SPLIT",FACE,{"disambiguationData":[TD([subQ20])],"derivedFrom":subQ17}),makeQuery(id+"F4.opExtrude","SWEPT_FACE",FACE,{"disambiguationData":[OSD([subQ6]),TDD([makeQuery(id+"F3.boolean.opBoolean","SPLIT",EDGE,{"disambiguationData":[TD([subQ20])],"derivedFrom":makeQuery(id+"F1.opExtrude","CAP_EDGE",EDGE,{"disambiguationData":[OSD([subQ6])],"isStart":false})})])]})]}),makeQuery(id+"F5.opExtrude","SWEPT_FACE",FACE,{"disambiguationData":[OSD([subQ5])]})]}),makeQuery(id+"F15.opExtrude","SWEPT_FACE",FACE,{"disambiguationData":[OSD([subQ6,subQ14,subQ13,subQ12,subQ2]),TDD([makeQuery(id+"F13.boolean.opBoolean","MERGE",EDGE,{"derivedFrom":[makeQuery(id+"F4.boolean.opBoolean","MERGE",EDGE,{"derivedFrom":[makeQuery(id+"F3.opExtrude","CAP_EDGE",EDGE,{"disambiguationData":[OSD([subQ14,subQ12])],"isStart":true}),makeQuery(id+"F4.opExtrude","SWEPT_EDGE",EDGE,{"disambiguationData":[OSD([subQ6,subQ14,subQ13]),TDD([makeQuery(id+"F3.opExtrude","CAP_VERTEX",VERTEX,{"disambiguationData":[OSD([subQ6,subQ14,subQ13])],"isStart":true})])]})]}),makeQuery(id+"F13.opExtrude","SWEPT_EDGE",EDGE,{"disambiguationData":[OSD([subQ12,subQ2]),TDD([makeQuery(id+"F3.opExtrude","CAP_VERTEX",VERTEX,{"disambiguationData":[OSD([subQ12,subQ2])],"isStart":true})])]})]})])]})]});Q1=makeQuery(id+"F34.boolean.opBoolean","MERGE",FACE,{"derivedFrom":[makeQuery(id+"F33.boolean.opBoolean","MERGE",FACE,{"derivedFrom":[makeQuery(id+"F31.boolean.opBoolean","SPLIT",FACE,{"disambiguationData":[TD([subQ20])],"derivedFrom":subQ21}),makeQuery(id+"F31.boolean.opBoolean","SPLIT",FACE,{"disambiguationData":[TD([makeQuery(id+"F31.opExtrude","SWEPT_FACE",FACE,{"disambiguationData":[OSD([sQuery(id+"F30.wireOp",EDGE,"E15.right")])]})])],"derivedFrom":subQ21}),makeQuery(id+"F33.opExtrude","SWEPT_FACE",FACE,{"disambiguationData":[OSD([subQ0])]})]}),makeQuery(id+"F34.opExtrude","SWEPT_FACE",FACE,{"disambiguationData":[OSD([subQ5,subQ4,subQ3,subQ2,sQuery(id+"F30.wireOp",EDGE,"E15.top"),subQ1,subQ0,sQuery(id+"F32.wireOp",EDGE,"E17.right")])]})]});}
            extrude(context, id + "F47", {"entities" : qUnion([Q0]), "operationType" : NewBodyOperationType.REMOVE, "endBound" : BoundingType.UP_TO_SURFACE, "oppositeDirection" : true, "endBoundEntityFace" : qUnion([Q1]), "depth" : 25.4 * mm});
        }
        {
            var Q0;
            {var subQ0=sQuery(id+"F2.wireOp",EDGE,"E4.right");var subQ1=sQuery(id+"F2.wireOp",EDGE,"E4.bottom");var subQ2=sQuery(id+"F2.wireOp",EDGE,"E2.left");var subQ3=sQuery(id+"F2.wireOp",EDGE,"E2.top");var subQ4=sQuery(id+"F0.wireOp",EDGE,"E0.right");Q0=makeQuery(id+"F42.boolean.opBoolean","MERGE",FACE,{"derivedFrom":[makeQuery(id+"F19.boolean.opBoolean","MERGE",FACE,{"derivedFrom":[makeQuery(id+"F15.boolean.opBoolean","COPY",FACE,{"derivedFrom":makeQuery(id+"F15.opExtrude","CAP_FACE",FACE,{"disambiguationData":[OSD([subQ4,subQ3,subQ2,subQ1,subQ0])],"isStart":false})}),makeQuery(id+"F19.opExtrude","SWEPT_FACE",FACE,{"disambiguationData":[OSD([subQ4,subQ3,subQ2,subQ1,subQ0,sQuery(id+"F16.wireOp",EDGE,"E9.top")])]})]}),makeQuery(id+"F42.opExtrude","SWEPT_FACE",FACE,{"disambiguationData":[OSD([subQ4,subQ3,subQ2,subQ1,subQ0,sQuery(id+"F16.wireOp",EDGE,"E9.bottom"),sQuery(id+"F16.wireOp",EDGE,"E9.left")])]})]});}
            var Q1;
            {var subQ0=sQuery(id+"F16.wireOp",EDGE,"E9.left");var subQ1=sQuery(id+"F16.wireOp",EDGE,"E9.bottom");var subQ2=sQuery(id+"F2.wireOp",EDGE,"E2.bottom");Q1=makeQuery(id+"F42.boolean.opBoolean","MERGE",FACE,{"derivedFrom":[makeQuery(id+"F19.boolean.opBoolean","MERGE",FACE,{"derivedFrom":[makeQuery(id+"F14.boolean.opBoolean","MERGE",FACE,{"derivedFrom":[makeQuery(id+"F4.boolean.opBoolean","MERGE",FACE,{"derivedFrom":[makeQuery(id+"F3.opExtrude","SWEPT_FACE",FACE,{"disambiguationData":[OSD([subQ2])]}),makeQuery(id+"F4.opExtrude","SWEPT_FACE",FACE,{"disambiguationData":[OSD([sQuery(id+"F0.wireOp",EDGE,"E0.right"),subQ2,sQuery(id+"F2.wireOp",EDGE,"E2.left")])]})]}),makeQuery(id+"F14.opExtrude","SWEPT_FACE",FACE,{"disambiguationData":[OSD([subQ2,sQuery(id+"F2.wireOp",EDGE,"E3.left"),sQuery(id+"F2.wireOp",EDGE,"E3.top"),sQuery(id+"F2.wireOp",EDGE,"E4.left")])]})]}),makeQuery(id+"F19.opExtrude","SWEPT_FACE",FACE,{"disambiguationData":[OSD([sQuery(id+"F16.wireOp",EDGE,"E9.top")])]})]}),makeQuery(id+"F42.opExtrude","SWEPT_FACE",FACE,{"disambiguationData":[OSD([subQ1,subQ0]),TDD([makeQuery(id+"F18.boolean.opBoolean","MERGE",EDGE,{"derivedFrom":[makeQuery(id+"F17.boolean.opBoolean","COPY",EDGE,{"derivedFrom":makeQuery(id+"F17.opExtrude","CAP_EDGE",EDGE,{"disambiguationData":[OSD([subQ0])],"isStart":true})}),makeQuery(id+"F18.opExtrude","SWEPT_EDGE",EDGE,{"disambiguationData":[OSD([subQ1,subQ0])]})]})])]})]});}
            extrude(context, id + "F48", {"entities" : qUnion([Q0]), "operationType" : NewBodyOperationType.REMOVE, "endBound" : BoundingType.UP_TO_SURFACE, "oppositeDirection" : true, "endBoundEntityFace" : qUnion([Q1]), "depth" : 25.4 * mm});
        }
        {
            var Q0;
            {var subQ0=sQuery(id+"F2.wireOp",EDGE,"E3.bottom");var subQ1=sQuery(id+"F0.wireOp",EDGE,"E0.top");Q0=makeQuery(id+"F13.boolean.opBoolean","MERGE",FACE,{"derivedFrom":[makeQuery(id+"F7.boolean.opBoolean","MERGE",FACE,{"derivedFrom":[makeQuery(id+"F5.opExtrude","CAP_FACE",FACE,{"disambiguationData":[OSD([subQ1,sQuery(id+"F0.wireOp",EDGE,"E0.right"),subQ0])],"isStart":false}),makeQuery(id+"F7.opExtrude","SWEPT_FACE",FACE,{"disambiguationData":[OSD([sQuery(id+"F6.wireOp",EDGE,"E5.top"),sQuery(id+"F6.wireOp",EDGE,"E6.bottom")])]})]}),makeQuery(id+"F13.opExtrude","SWEPT_FACE",FACE,{"disambiguationData":[OSD([subQ1,subQ0,sQuery(id+"F2.wireOp",EDGE,"E3.right")])]})]});}
            var Q1;
            {var subQ0=sQuery(id+"F6.wireOp",EDGE,"E6.top");Q1=makeQuery(id+"F14.boolean.opBoolean","MERGE",FACE,{"derivedFrom":[makeQuery(id+"F12.boolean.opBoolean","MERGE",FACE,{"derivedFrom":[makeQuery(id+"F7.opExtrude","SWEPT_FACE",FACE,{"disambiguationData":[OSD([subQ0])]}),makeQuery(id+"F12.opExtrude","SWEPT_FACE",FACE,{"disambiguationData":[OSD([subQ0,sQuery(id+"F9.wireOp",EDGE,"E7.bottom"),sQuery(id+"F9.wireOp",EDGE,"E7.right")])]})]}),makeQuery(id+"F14.opExtrude","SWEPT_FACE",FACE,{"disambiguationData":[OSD([sQuery(id+"F0.wireOp",EDGE,"E0.top"),sQuery(id+"F2.wireOp",EDGE,"E3.bottom"),sQuery(id+"F2.wireOp",EDGE,"E3.left"),subQ0,sQuery(id+"F6.wireOp",EDGE,"E6.left")])]})]});}
            extrude(context, id + "F49", {"entities" : qUnion([Q0, Q1]), "operationType" : NewBodyOperationType.REMOVE, "oppositeDirection" : true, "depth" : 25.4 * mm});
        }
        {
            var Q0;
            Q0=makeQuery(id+"F49.boolean.opBoolean","COPY",FACE,{"derivedFrom":makeQuery(id+"F49.opExtrude","CAP_FACE",FACE,{"disambiguationData":[OSD([sQuery(id+"F0.wireOp",EDGE,"E0.top"),sQuery(id+"F0.wireOp",EDGE,"E0.right"),sQuery(id+"F2.wireOp",EDGE,"E3.bottom"),sQuery(id+"F2.wireOp",EDGE,"E3.right"),sQuery(id+"F6.wireOp",EDGE,"E5.top"),sQuery(id+"F6.wireOp",EDGE,"E6.bottom")])],"isStart":false})});
            var Q1;
            {var subQ0=sQuery(id+"F6.wireOp",EDGE,"E6.top");Q1=makeQuery(id+"F14.boolean.opBoolean","MERGE",FACE,{"derivedFrom":[makeQuery(id+"F12.boolean.opBoolean","MERGE",FACE,{"derivedFrom":[makeQuery(id+"F7.opExtrude","SWEPT_FACE",FACE,{"disambiguationData":[OSD([subQ0])]}),makeQuery(id+"F12.opExtrude","SWEPT_FACE",FACE,{"disambiguationData":[OSD([subQ0,sQuery(id+"F9.wireOp",EDGE,"E7.bottom"),sQuery(id+"F9.wireOp",EDGE,"E7.right")])]})]}),makeQuery(id+"F14.opExtrude","SWEPT_FACE",FACE,{"disambiguationData":[OSD([sQuery(id+"F0.wireOp",EDGE,"E0.top"),sQuery(id+"F2.wireOp",EDGE,"E3.bottom"),sQuery(id+"F2.wireOp",EDGE,"E3.left"),subQ0,sQuery(id+"F6.wireOp",EDGE,"E6.left")])]})]});}
            extrude(context, id + "F50", {"entities" : qUnion([Q0]), "operationType" : NewBodyOperationType.REMOVE, "endBound" : BoundingType.UP_TO_SURFACE, "oppositeDirection" : true, "endBoundEntityFace" : qUnion([Q1]), "depth" : 25.4 * mm});
        }
        {
            var Q0;
            Q0=makeQuery(id+"F14.boolean.opBoolean","COPY",FACE,{"derivedFrom":makeQuery(id+"F14.opExtrude","CAP_FACE",FACE,{"disambiguationData":[OSD([sQuery(id+"F0.wireOp",EDGE,"E0.top"),sQuery(id+"F2.wireOp",EDGE,"E3.bottom"),sQuery(id+"F2.wireOp",EDGE,"E3.left")])],"isStart":false})});
            var Q1;
            {var subQ0=sQuery(id+"F2.wireOp",EDGE,"E4.right");var subQ1=sQuery(id+"F2.wireOp",EDGE,"E3.right");var subQ2=sQuery(id+"F2.wireOp",EDGE,"E3.bottom");var subQ3=sQuery(id+"F0.wireOp",EDGE,"E0.top");Q1=makeQuery(id+"F31.boolean.opBoolean","SPLIT",FACE,{"disambiguationData":[TD([makeQuery(id+"F31.opExtrude","SWEPT_FACE",FACE,{"disambiguationData":[OSD([sQuery(id+"F30.wireOp",EDGE,"E15.right")])]})])],"derivedFrom":makeQuery(id+"F13.opExtrude","CAP_FACE",FACE,{"disambiguationData":[OSD([subQ3,subQ2,subQ1,subQ0])],"isStart":false})});}
            extrude(context, id + "F51", {"entities" : qUnion([Q0]), "operationType" : NewBodyOperationType.REMOVE, "endBound" : BoundingType.UP_TO_SURFACE, "oppositeDirection" : true, "endBoundEntityFace" : qUnion([Q1]), "depth" : 25.4 * mm});
        }
        {
            var Q0;
            Q0=makeQuery(id+"F35.boolean.opBoolean","MERGE",FACE,{"derivedFrom":[makeQuery(id+"F31.opExtrude","SWEPT_FACE",FACE,{"disambiguationData":[OSD([sQuery(id+"F30.wireOp",EDGE,"E15.left")])]}),makeQuery(id+"F35.opExtrude","SWEPT_FACE",FACE,{"disambiguationData":[OSD([sQuery(id+"F32.wireOp",EDGE,"E17.left")])]})]});
            var Q1;
            {var subQ0=sQuery(id+"F30.wireOp",EDGE,"E15.right");Q1=makeQuery(id+"F35.boolean.opBoolean","MERGE",FACE,{"derivedFrom":[makeQuery(id+"F31.opExtrude","SWEPT_FACE",FACE,{"disambiguationData":[OSD([subQ0])]}),makeQuery(id+"F35.opExtrude","SWEPT_FACE",FACE,{"disambiguationData":[OSD([subQ0,sQuery(id+"F32.wireOp",EDGE,"E17.left")])]})]});}
            extrude(context, id + "F52", {"entities" : qUnion([Q0]), "operationType" : NewBodyOperationType.REMOVE, "endBound" : BoundingType.UP_TO_SURFACE, "oppositeDirection" : true, "endBoundEntityFace" : qUnion([Q1]), "depth" : 25.4 * mm});
        }
        {
            var Q0;
            {var subQ0=sQuery(id+"F22.wireOp",EDGE,"E13.right");var subQ1=sQuery(id+"F22.wireOp",EDGE,"E13.left");Q0=makeQuery(id+"F45.boolean.opBoolean","MERGE",FACE,{"derivedFrom":[makeQuery(id+"F39.boolean.opBoolean","MERGE",FACE,{"derivedFrom":[makeQuery(id+"F36.boolean.opBoolean","MERGE",FACE,{"derivedFrom":[makeQuery(id+"F29.boolean.opBoolean","MERGE",FACE,{"derivedFrom":[makeQuery(id+"F26.boolean.opBoolean","MERGE",FACE,{"derivedFrom":[makeQuery(id+"F25.boolean.opBoolean","MERGE",FACE,{"derivedFrom":[makeQuery(id+"F7.opExtrude","SWEPT_FACE",FACE,{"disambiguationData":[OSD([sQuery(id+"F6.wireOp",EDGE,"E5.right")])]}),makeQuery(id+"F25.opExtrude","SWEPT_FACE",FACE,{"disambiguationData":[OSD([subQ1])]})]}),makeQuery(id+"F26.opExtrude","SWEPT_FACE",FACE,{"disambiguationData":[OSD([subQ0])]})]}),makeQuery(id+"F29.opExtrude","SWEPT_FACE",FACE,{"disambiguationData":[OSD([subQ0])]})]}),makeQuery(id+"F36.opExtrude","SWEPT_FACE",FACE,{"disambiguationData":[OSD([sQuery(id+"F22.wireOp",EDGE,"E13.top"),subQ1,subQ0])]})]}),makeQuery(id+"F39.opExtrude","SWEPT_FACE",FACE,{"disambiguationData":[OSD([sQuery(id+"F20.wireOp",EDGE,"E11.bottom")])]})]}),makeQuery(id+"F45.opExtrude","SWEPT_FACE",FACE,{"disambiguationData":[OSD([sQuery(id+"F20.wireOp",EDGE,"E11.top")])]})]});}
            var sketch = newSketch(context, id + "F53", { "sketchPlane" : qUnion([Q0])});
            skLineSegment(sketch, "E18.bottom", {"start": v(-4216.2, 2451.9) * mm, "end": v(-3797.3, 2451.9) * mm, "construction": true});
            skLineSegment(sketch, "E18.top", {"start": v(-4216.2, 2477.3) * mm, "end": v(-3797.3, 2477.3) * mm, "construction": true});
            skLineSegment(sketch, "E18.left", {"start": v(-4216.2, 2451.9) * mm, "end": v(-4216.2, 2477.3) * mm, "construction": true});
            skLineSegment(sketch, "E18.right", {"start": v(-3797.3, 2451.9) * mm, "end": v(-3797.3, 2477.3) * mm, "construction": true});
            skLineSegment(sketch, "E19.top", {"start": v(-4216.2, 2558.57) * mm, "end": v(-3797.3, 2558.57) * mm, "construction": true});
            skLineSegment(sketch, "E19.left", {"start": v(-4216.2, 2477.3) * mm, "end": v(-4216.2, 2558.57) * mm, "construction": true});
            skLineSegment(sketch, "E19.right", {"start": v(-3797.3, 2477.3) * mm, "end": v(-3797.3, 2558.57) * mm, "construction": true});
            skLineSegment(sketch, "E20.bottom", {"start": v(-3797.3, 2477.3) * mm, "end": v(-3794.76, 2477.3) * mm});
            skLineSegment(sketch, "E20.top", {"start": v(-3797.3, 2561.11) * mm, "end": v(-3794.76, 2561.11) * mm});
            skLineSegment(sketch, "E20.left", {"start": v(-3797.3, 2477.3) * mm, "end": v(-3797.3, 2561.11) * mm});
            skLineSegment(sketch, "E20.right", {"start": v(-3794.76, 2477.3) * mm, "end": v(-3794.76, 2561.11) * mm});
            skLineSegment(sketch, "E21.bottom", {"start": v(-4216.2, 2477.3) * mm, "end": v(-4218.74, 2477.3) * mm});
            skLineSegment(sketch, "E21.top", {"start": v(-4216.2, 2561.11) * mm, "end": v(-4218.74, 2561.11) * mm});
            skLineSegment(sketch, "E21.left", {"start": v(-4216.2, 2477.3) * mm, "end": v(-4216.2, 2561.11) * mm});
            skLineSegment(sketch, "E21.right", {"start": v(-4218.74, 2477.3) * mm, "end": v(-4218.74, 2561.11) * mm});
            skLineSegment(sketch, "E22.bottom", {"start": v(-4216.2, 2561.11) * mm, "end": v(-3797.3, 2561.11) * mm});
            skLineSegment(sketch, "E22.top", {"start": v(-4216.2, 2558.57) * mm, "end": v(-3797.3, 2558.57) * mm});
            skLineSegment(sketch, "E22.left", {"start": v(-4216.2, 2561.11) * mm, "end": v(-4216.2, 2558.57) * mm});
            skLineSegment(sketch, "E22.right", {"start": v(-3797.3, 2561.11) * mm, "end": v(-3797.3, 2558.57) * mm});
            skSolve(sketch);
        }
        {
            var Q0;
            Q0=makeQuery(id+"F53.imprint","IMPRINT",FACE,{"disambiguationData":[TD([[makeQuery(id+"F53.imprint","IMPRINT",EDGE,{"derivedFrom":sQuery(id+"F53.wireOp",EDGE,"E22.bottom")}),-1.0]])]});
            var Q1;
            Q1=makeQuery(id+"F53.imprint","IMPRINT",FACE,{"disambiguationData":[TD([[makeQuery(id+"F53.imprint","IMPRINT",EDGE,{"derivedFrom":sQuery(id+"F53.wireOp",EDGE,"E20.bottom")}),1.0]])]});
            var Q2;
            Q2=makeQuery(id+"F53.imprint","IMPRINT",FACE,{"disambiguationData":[TD([[makeQuery(id+"F53.imprint","IMPRINT",EDGE,{"derivedFrom":sQuery(id+"F53.wireOp",EDGE,"E21.bottom")}),-1.0]])]});
            extrude(context, id + "F54", {"entities" : qUnion([Q0, Q1, Q2]), "oppositeDirection" : true, "depth" : 127 * mm});
        }
    });
